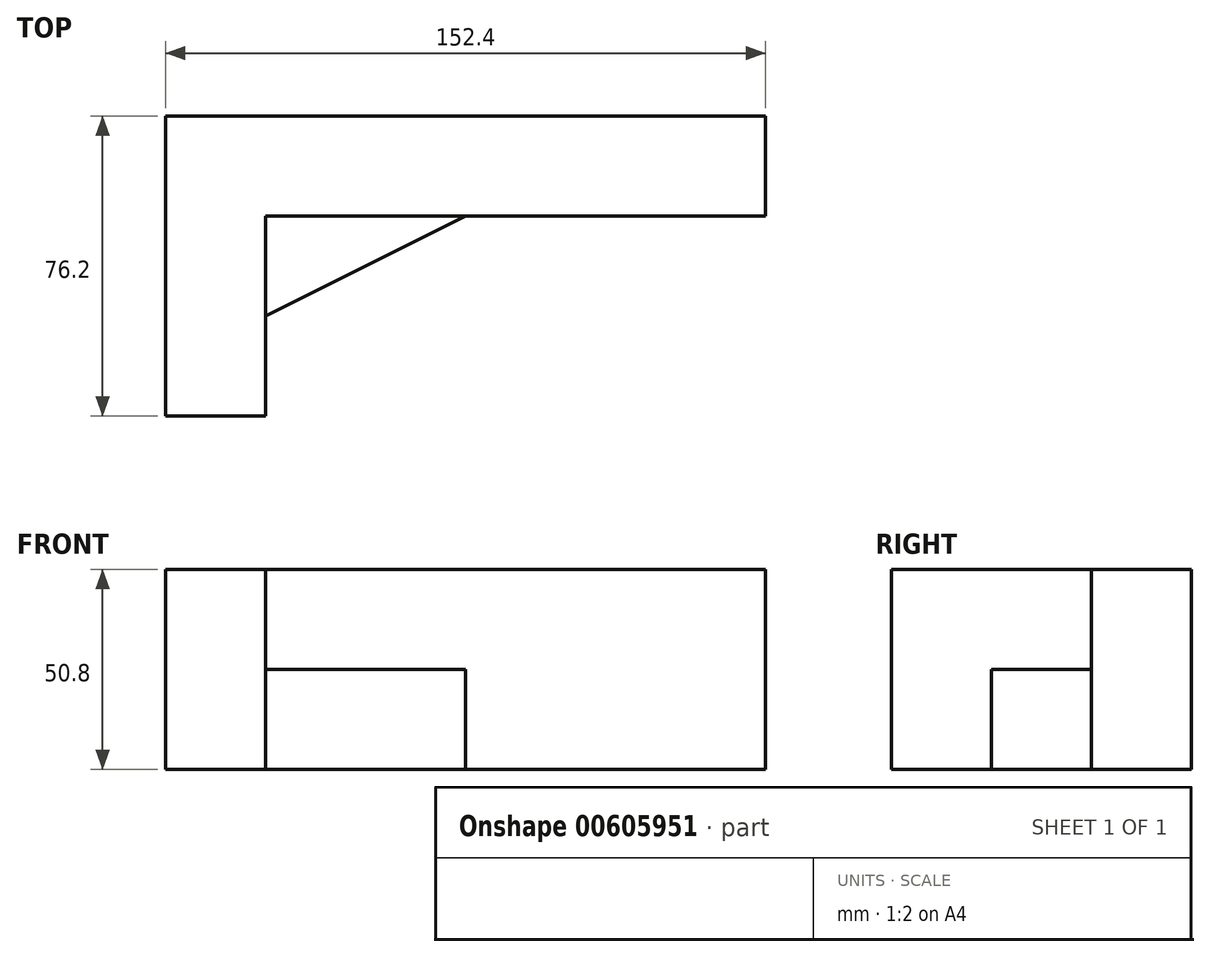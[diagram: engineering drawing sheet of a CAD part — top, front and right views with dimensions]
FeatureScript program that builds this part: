
annotation { "Feature Type Name" : "Feature", "Feature Type Description" : "" }
export const myFeature = defineFeature(function(context is Context, id is Id, definition is map)
    precondition{}
    {
        {
            var Q0;
            Q0=qCreatedBy(makeId("Front.planeOp"),FACE);
            var sketch = newSketch(context, id + "F0", { "sketchPlane" : qUnion([Q0])});
            skLineSegment(sketch, "E0", {"start": v(0, 0) * mm, "end": v(0, 50.8) * mm});
            skLineSegment(sketch, "E1", {"start": v(0, 50.8) * mm, "end": v(152.4, 50.8) * mm});
            skLineSegment(sketch, "E2", {"start": v(152.4, 50.8) * mm, "end": v(152.4, 0) * mm});
            skLineSegment(sketch, "E3", {"start": v(152.4, 0) * mm, "end": v(0, 0) * mm});
            skSolve(sketch);
        }
        {
            var Q0;
            Q0=makeQuery(id+"F0.imprint","IMPRINT",FACE,{"disambiguationData":[TD([[makeQuery(id+"F0.imprint","IMPRINT",EDGE,{"derivedFrom":sQuery(id+"F0.wireOp",EDGE,"E0")}),-1.0]])]});
            extrude(context, id + "F1", {"entities" : qUnion([Q0]), "depth" : 76.2 * mm, "offsetDistance" : 25.4 * mm});
        }
        {
            var Q0;
            Q0=makeQuery(id+"F1.opExtrude","SWEPT_FACE",FACE,{"disambiguationData":[OSD([sQuery(id+"F0.wireOp",EDGE,"E1")])]});
            var sketch = newSketch(context, id + "F2", { "sketchPlane" : qUnion([Q0])});
            skLineSegment(sketch, "E4", {"start": v(0, -76.2) * mm, "end": v(25.4, -76.2) * mm});
            skLineSegment(sketch, "E5", {"start": v(25.4, -76.2) * mm, "end": v(25.4, -25.4) * mm});
            skLineSegment(sketch, "E6", {"start": v(25.4, -25.4) * mm, "end": v(152.4, -25.4) * mm});
            skLineSegment(sketch, "E7", {"start": v(152.4, -25.4) * mm, "end": v(152.4, 0) * mm});
            skLineSegment(sketch, "E8", {"start": v(25.4, -50.8) * mm, "end": v(76.2, -50.8) * mm});
            skLineSegment(sketch, "E9", {"start": v(76.2, -50.8) * mm, "end": v(76.2, -25.4) * mm});
            skSolve(sketch);
        }
        {
            var Q0;
            {var subQ5=sQuery(id+"F2.wireOp",EDGE,"E8");Q0=makeQuery(id+"F2.imprint","IMPRINT",FACE,{"disambiguationData":[TD([[makeQuery(id+"F2.imprint","IMPRINT",EDGE,{"derivedFrom":subQ5}),-1.0]])]});}
            extrude(context, id + "F3", {"entities" : qUnion([Q0]), "operationType" : NewBodyOperationType.REMOVE, "oppositeDirection" : true, "depth" : 50.8 * mm, "offsetDistance" : 25.4 * mm});
        }
        {
            var Q0;
            Q0=makeQuery(id+"F1.opExtrude","SWEPT_FACE",FACE,{"disambiguationData":[OSD([sQuery(id+"F0.wireOp",EDGE,"E1")])]});
            var sketch = newSketch(context, id + "F4", { "sketchPlane" : qUnion([Q0])});
            skLineSegment(sketch, "E10", {"start": v(25.4, -50.8) * mm, "end": v(76.2, -25.4) * mm});
            skLineSegment(sketch, "E11", {"start": v(76.2, -25.4) * mm, "end": v(25.4, -25.4) * mm});
            skLineSegment(sketch, "E12", {"start": v(25.4, -25.4) * mm, "end": v(25.4, -50.8) * mm});
            skSolve(sketch);
        }
        {
            var Q0;
            Q0=makeQuery(id+"F4.imprint","IMPRINT",FACE,{"disambiguationData":[TD([[makeQuery(id+"F4.imprint","IMPRINT",EDGE,{"derivedFrom":sQuery(id+"F4.wireOp",EDGE,"E10")}),-1.0]])]});
            extrude(context, id + "F5", {"entities" : qUnion([Q0]), "operationType" : NewBodyOperationType.REMOVE, "oppositeDirection" : true, "depth" : 50.8 * mm, "offsetDistance" : 25.4 * mm});
        }
        {
            var Q0;
            Q0=makeQuery(id+"F1.opExtrude","SWEPT_FACE",FACE,{"disambiguationData":[OSD([sQuery(id+"F0.wireOp",EDGE,"E1")])]});
            var sketch = newSketch(context, id + "F6", { "sketchPlane" : qUnion([Q0])});
            skLineSegment(sketch, "E13", {"start": v(25.4, -50.8) * mm, "end": v(25.4, -25.4) * mm});
            skLineSegment(sketch, "E14", {"start": v(25.4, -25.4) * mm, "end": v(76.2, -25.4) * mm});
            skSolve(sketch);
        }
        {
            var Q0;
            Q0=makeQuery(id+"F6.imprint","IMPRINT",FACE,{"disambiguationData":[TD([[makeQuery(id+"F6.imprint","IMPRINT",EDGE,{"derivedFrom":sQuery(id+"F6.wireOp",EDGE,"E13")}),-1.0]])]});
            extrude(context, id + "F7", {"entities" : qUnion([Q0]), "operationType" : NewBodyOperationType.REMOVE, "oppositeDirection" : true, "depth" : 25.4 * mm, "offsetDistance" : 25.4 * mm});
        }
    });
